# Revit family: Base_Cabinets-Teknion-RHBSW_Base_Cabinet_for_Waste_and_Recycle_Bin-R2018
name_source: partatom
category: Furniture
revit_build: Autodesk Revit 2018 (Build: 20170223_1515(x64)
units: mm (PartAtom-declared; Revit-internal decimal feet)

## family parameters
Always vertical = Yes
Cut with Voids When Loaded = No
OmniClass Number = 23.40.20.00
OmniClass Title = General Furniture and Specialties
Room Calculation Point = No
Shared = Yes
Work Plane-Based = No

## types (4) — shared parameters
Assembly Code = E2020200
Manufacturer = Teknion
Manufacturer Fax = 416.661.4586
Part Number = RHBSW
Product Documentation Link = https://www.teknion.com
Product Line = Modular Cabinets
Product Page URL = https://www.teknion.com
Series = Modular Cabinets
Sustainability Data = https://www.teknion.com
URL = www.teknion.com
Unit Weight URL = http://www.teknion.com
Warranty = http://www.teknion.com

## per-type parameters (varying)
| type | Depth | Description | Height | Model | Top of Door Height Offset |
| 24" Depth, 33" Height | 24 " | Base Cabinet for Waste and Recycle Bin, 24" Depth, 33" Height | 32.5 " | RHBSW24__33 | 7.13 " |
| 24" Depth, 35" Height | 24 " | Base Cabinet for Waste and Recycle Bin, 24" Depth, 35" Height | 35 " | RHBSW24__35 | 7.756 " |
| 29" Depth, 33" Height | 29 " | Base Cabinet for Waste and Recycle Bin, 29" Depth, 33" Height | 32.5 " | RHBSW29__33 | 7.13 " |
| 29" Depth, 35" Height | 29 " | Base Cabinet for Waste and Recycle Bin, 29" Depth, 35" Height | 35 " | RHBSW29__35 | 7.756 " |

## geometry (parser evidence)
native form markers: Sweep x2
no freeform markers — native parametric forms only
